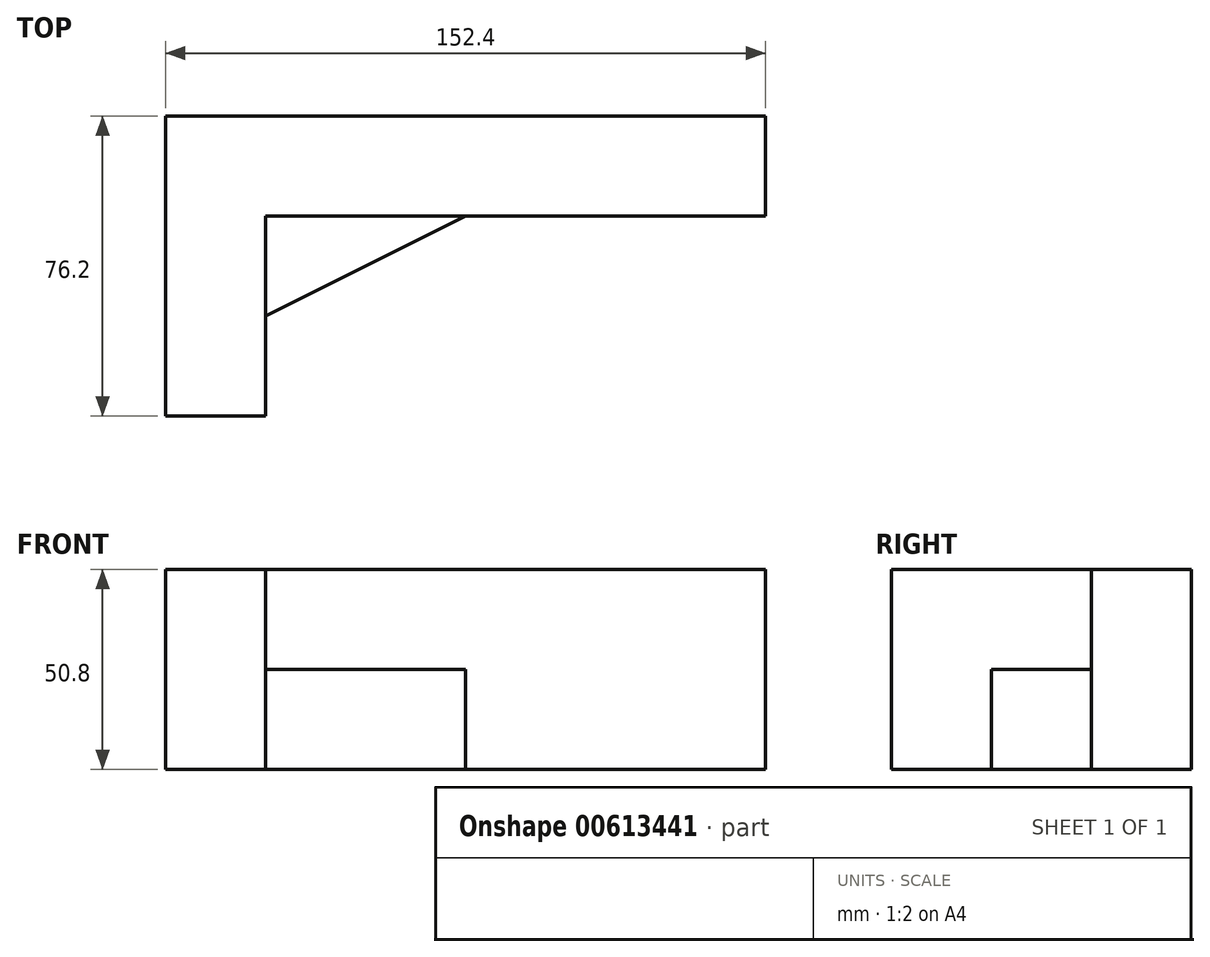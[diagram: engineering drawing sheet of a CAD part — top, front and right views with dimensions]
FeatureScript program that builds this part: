
annotation { "Feature Type Name" : "Feature", "Feature Type Description" : "" }
export const myFeature = defineFeature(function(context is Context, id is Id, definition is map)
    precondition{}
    {
        {
            var Q0;
            Q0=qCreatedBy(makeId("Top.planeOp"),FACE);
            var sketch = newSketch(context, id + "F0", { "sketchPlane" : qUnion([Q0])});
            skLineSegment(sketch, "E0", {"start": v(-81.92, 38.97) * mm, "end": v(-81.92, -37.23) * mm});
            skLineSegment(sketch, "E1", {"start": v(-81.92, -37.23) * mm, "end": v(-56.52, -37.23) * mm});
            skLineSegment(sketch, "E2", {"start": v(-56.52, -37.23) * mm, "end": v(-56.52, 13.57) * mm});
            skLineSegment(sketch, "E3", {"start": v(-56.52, 13.57) * mm, "end": v(70.48, 13.57) * mm});
            skLineSegment(sketch, "E4", {"start": v(70.48, 13.57) * mm, "end": v(70.48, 38.97) * mm});
            skLineSegment(sketch, "E5", {"start": v(70.48, 38.97) * mm, "end": v(-81.92, 38.97) * mm});
            skSolve(sketch);
        }
        {
            var Q0;
            Q0 = qSketchRegion(id + "F0", true);
            extrude(context, id + "F1", {"entities" : qUnion([Q0]), "depth" : 50.8 * mm, "offsetDistance" : 25.4 * mm});
        }
        {
            var Q0;
            Q0=makeQuery(id+"F1.opExtrude","CAP_FACE",FACE,{"disambiguationData":[OSD([sQuery(id+"F0.wireOp",EDGE,"E0"),sQuery(id+"F0.wireOp",EDGE,"E1"),sQuery(id+"F0.wireOp",EDGE,"E2"),sQuery(id+"F0.wireOp",EDGE,"E3"),sQuery(id+"F0.wireOp",EDGE,"E4"),sQuery(id+"F0.wireOp",EDGE,"E5")])],"isStart":true});
            var sketch = newSketch(context, id + "F2", { "sketchPlane" : qUnion([Q0])});
            skLineSegment(sketch, "E6", {"start": v(-56.52, 11.83) * mm, "end": v(-5.72, -13.57) * mm});
            skSolve(sketch);
        }
        {
            var Q0;
            Q0 = qSketchRegion(id + "F2", true);
            var Q1;
            {var subQ0=sQuery(id+"F2.wireOp",EDGE,"E6");Q1=makeQuery(id+"F2.imprint","IMPRINT",FACE,{"disambiguationData":[TD([[makeQuery(id+"F2.imprint","IMPRINT",EDGE,{"derivedFrom":subQ0}),-1.0]])]});}
            extrude(context, id + "F3", {"entities" : qUnion([Q0, Q1]), "operationType" : NewBodyOperationType.ADD, "oppositeDirection" : true, "depth" : 25.4 * mm, "offsetDistance" : 25.4 * mm});
        }
    });
